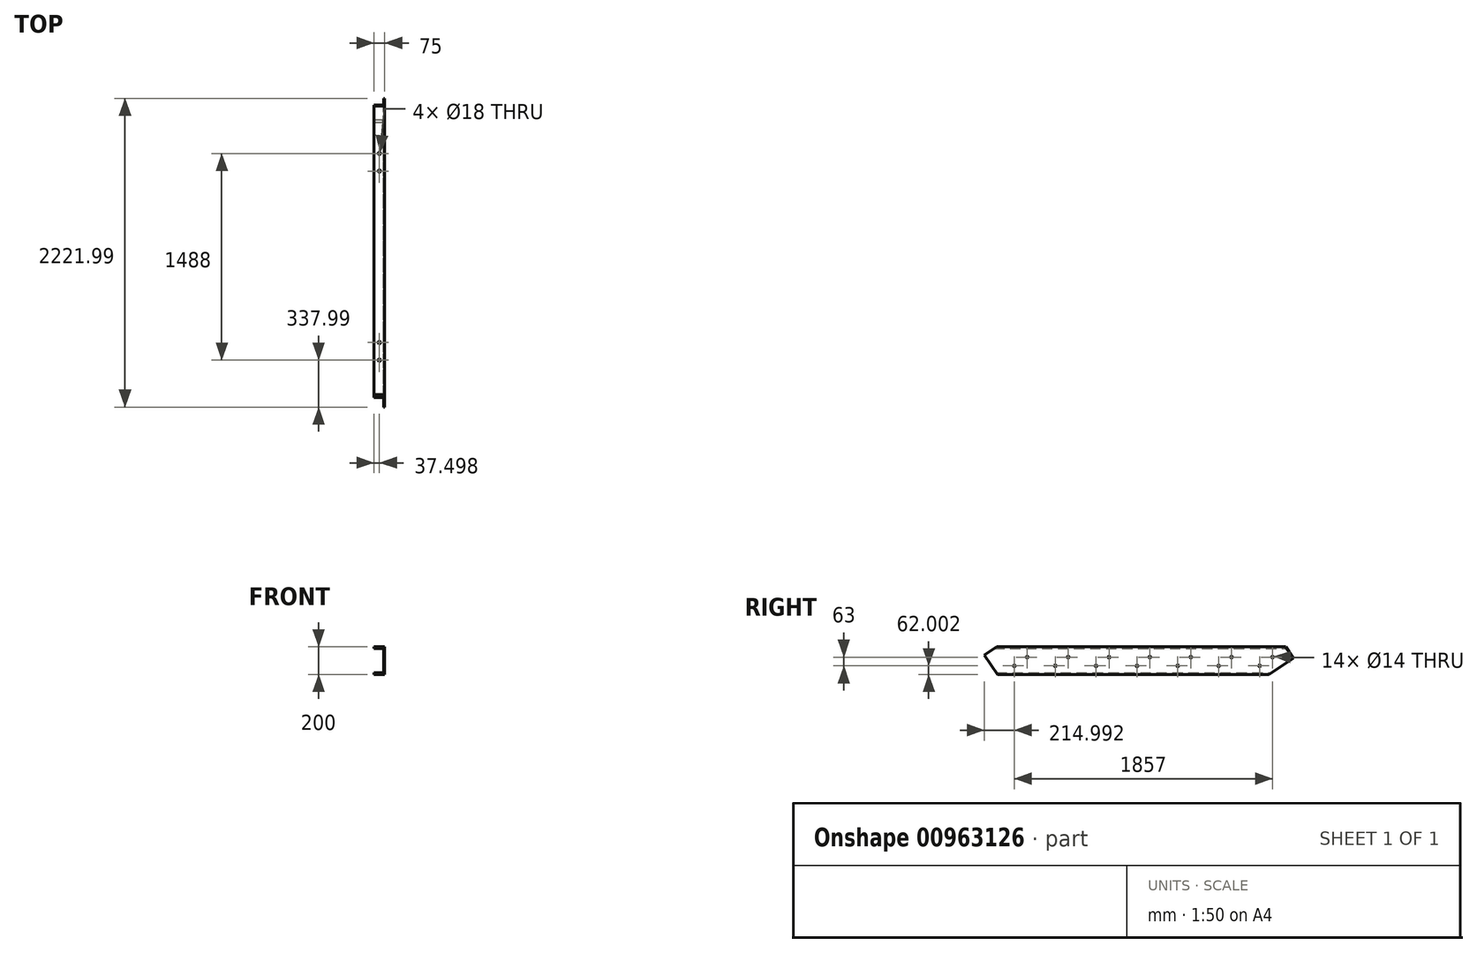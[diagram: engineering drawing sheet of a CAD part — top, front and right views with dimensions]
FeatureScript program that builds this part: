
annotation { "Feature Type Name" : "Feature", "Feature Type Description" : "" }
export const myFeature = defineFeature(function(context is Context, id is Id, definition is map)
    precondition{}
    {
        {
            var Q0;
            Q0=qCreatedBy(makeId("Front.planeOp"),FACE);
            var sketch = newSketch(context, id + "F0", { "sketchPlane" : qUnion([Q0])});
            skLineSegment(sketch, "E0", {"start": v(-161.38, 109) * mm, "end": v(-86.38, 109) * mm});
            skLineSegment(sketch, "E1", {"start": v(-86.38, 109) * mm, "end": v(-86.38, -91) * mm});
            skLineSegment(sketch, "E2", {"start": v(-86.38, -91) * mm, "end": v(-161.38, -91) * mm});
            skLineSegment(sketch, "E3.0", {"start": v(-92.38, 84.5) * mm, "end": v(-92.38, -66.5) * mm});
            skLineSegment(sketch, "E4.0", {"start": v(-161.38, 96.5) * mm, "end": v(-104.38, 96.5) * mm});
            skLineSegment(sketch, "E5.0", {"start": v(-104.38, -78.5) * mm, "end": v(-161.38, -78.5) * mm});
            skLineSegment(sketch, "E6", {"start": v(-161.38, 109) * mm, "end": v(-161.38, 96.5) * mm});
            skLineSegment(sketch, "E7", {"start": v(-161.38, -78.5) * mm, "end": v(-161.38, -91) * mm});
            skArc(sketch, "E8.filletArc", {"start": v(-104.38, -78.5) * mm, "mid": v(-95.9, -74.98) * mm, "end": v(-92.38, -66.5) * mm});
            skArc(sketch, "E9.filletArc", {"start": v(-92.38, 84.5) * mm, "mid": v(-95.9, 93) * mm, "end": v(-104.38, 96.5) * mm});
            skSolve(sketch);
        }
        {
            var Q0;
            Q0 = qSketchRegion(id + "F0", true);
            extrude(context, id + "F1", {"entities" : qUnion([Q0]), "depth" : 2222 * mm, "offsetDistance" : 25 * mm});
        }
        {
            var Q0;
            Q0=makeQuery(id+"F1.opExtrude","SWEPT_FACE",FACE,{"disambiguationData":[OSD([sQuery(id+"F0.wireOp",EDGE,"E7")])]});
            var sketch = newSketch(context, id + "F2", { "sketchPlane" : qUnion([Q0])});
            skLineSegment(sketch, "E10", {"start": v(0, 109.01) * mm, "end": v(0, 26.01) * mm});
            skLineSegment(sketch, "E11", {"start": v(0, 109.01) * mm, "end": v(56, 109.01) * mm});
            skLineSegment(sketch, "E12", {"start": v(56, 109.01) * mm, "end": v(0, 26.01) * mm});
            skLineSegment(sketch, "E13", {"start": v(0, -90.99) * mm, "end": v(174, -90.99) * mm});
            skLineSegment(sketch, "E14", {"start": v(174, -90.99) * mm, "end": v(0, 26.01) * mm});
            skLineSegment(sketch, "E15", {"start": v(0, 109.01) * mm, "end": v(150, 109.01) * mm});
            skLineSegment(sketch, "E16", {"start": v(150, 109.01) * mm, "end": v(243, 109.01) * mm});
            skCircle(sketch, "E17", {"center": v(150, 34.01) * mm, "radius": 7 * mm});
            skCircle(sketch, "E18", {"center": v(243, -28.99) * mm, "radius": 7 * mm});
            skCircle(sketch, "E19.1.0.0", {"center": v(444, 34.01) * mm, "radius": 7 * mm});
            skCircle(sketch, "E19.1.0.1", {"center": v(537, -28.99) * mm, "radius": 7 * mm});
            skCircle(sketch, "E19.2.0.0", {"center": v(738, 34.01) * mm, "radius": 7 * mm});
            skCircle(sketch, "E19.2.0.1", {"center": v(831, -28.99) * mm, "radius": 7 * mm});
            skCircle(sketch, "E19.3.0.0", {"center": v(1032, 34.01) * mm, "radius": 7 * mm});
            skCircle(sketch, "E19.3.0.1", {"center": v(1125, -28.99) * mm, "radius": 7 * mm});
            skCircle(sketch, "E19.4.0.0", {"center": v(1326, 34.01) * mm, "radius": 7 * mm});
            skCircle(sketch, "E19.4.0.1", {"center": v(1419, -28.99) * mm, "radius": 7 * mm});
            skCircle(sketch, "E19.5.0.0", {"center": v(1620, 34.01) * mm, "radius": 7 * mm});
            skCircle(sketch, "E19.5.0.1", {"center": v(1713, -28.99) * mm, "radius": 7 * mm});
            skCircle(sketch, "E19.6.0.0", {"center": v(1914, 34.01) * mm, "radius": 7 * mm});
            skCircle(sketch, "E19.6.0.1", {"center": v(2007, -28.99) * mm, "radius": 7 * mm});
            skLineSegment(sketch, "E19.direction1", {"start": v(150, 34.01) * mm, "end": v(444, 34.01) * mm, "construction": true});
            skLineSegment(sketch, "E20", {"start": v(2222, 109.01) * mm, "end": v(2134, 109.01) * mm});
            skLineSegment(sketch, "E21", {"start": v(2222, 109.01) * mm, "end": v(2222, 50.01) * mm});
            skLineSegment(sketch, "E22", {"start": v(2222, 50.01) * mm, "end": v(2134, 109.01) * mm});
            skLineSegment(sketch, "E23", {"start": v(2222, -90.99) * mm, "end": v(2127, -90.99) * mm});
            skLineSegment(sketch, "E24", {"start": v(2127, -90.99) * mm, "end": v(2222, 50.01) * mm});
            skLineSegment(sketch, "E25", {"start": v(0, 26.01) * mm, "end": v(0, -90.99) * mm});
            skLineSegment(sketch, "E26", {"start": v(2222, 50.01) * mm, "end": v(2222, -90.99) * mm});
            skSolve(sketch);
        }
        {
            var Q0;
            {var subQ0=sQuery(id+"F2.wireOp",EDGE,"E10");Q0=makeQuery(id+"F2.imprint","IMPRINT",FACE,{"disambiguationData":[TD([[makeQuery(id+"F2.imprint","IMPRINT",EDGE,{"derivedFrom":subQ0}),1.0]])]});}
            var Q1;
            {var subQ1=sQuery(id+"F2.wireOp",EDGE,"E14");var subQ3=makeQuery(id+"F1.opExtrude","SWEPT_EDGE",EDGE,{"disambiguationData":[OSD([sQuery(id+"F0.wireOp",EDGE,"E5.0"),sQuery(id+"F0.wireOp",EDGE,"E7")])]});var subQ4=makeQuery(id+"F2.imprint","INTERSECT",VERTEX,{"derivedFrom":[subQ3,subQ1]});Q1=makeQuery(id+"F2.imprint","IMPRINT",FACE,{"disambiguationData":[TD([[makeQuery(id+"F2.imprint","IMPRINT",EDGE,{"disambiguationData":[TD([[subQ4,-1.0]])],"derivedFrom":subQ1}),1.0]])]});}
            var Q2;
            {var subQ0=sQuery(id+"F2.wireOp",EDGE,"E13");Q2=makeQuery(id+"F2.imprint","IMPRINT",FACE,{"disambiguationData":[TD([[makeQuery(id+"F2.imprint","IMPRINT",EDGE,{"derivedFrom":subQ0}),1.0]])]});}
            var Q3;
            Q3=makeQuery(id+"F2.imprint","IMPRINT",FACE,{"disambiguationData":[TD([[makeQuery(id+"F2.imprint","IMPRINT",EDGE,{"derivedFrom":sQuery(id+"F2.wireOp",EDGE,"E17")}),1.0]])]});
            var Q4;
            Q4=makeQuery(id+"F2.imprint","IMPRINT",FACE,{"disambiguationData":[TD([[makeQuery(id+"F2.imprint","IMPRINT",EDGE,{"derivedFrom":sQuery(id+"F2.wireOp",EDGE,"E18")}),1.0]])]});
            var Q5;
            Q5=makeQuery(id+"F2.imprint","IMPRINT",FACE,{"disambiguationData":[TD([[makeQuery(id+"F2.imprint","IMPRINT",EDGE,{"derivedFrom":sQuery(id+"F2.wireOp",EDGE,"E19.1.0.0")}),1.0]])]});
            var Q6;
            Q6=makeQuery(id+"F2.imprint","IMPRINT",FACE,{"disambiguationData":[TD([[makeQuery(id+"F2.imprint","IMPRINT",EDGE,{"derivedFrom":sQuery(id+"F2.wireOp",EDGE,"E19.1.0.1")}),1.0]])]});
            var Q7;
            Q7=makeQuery(id+"F2.imprint","IMPRINT",FACE,{"disambiguationData":[TD([[makeQuery(id+"F2.imprint","IMPRINT",EDGE,{"derivedFrom":sQuery(id+"F2.wireOp",EDGE,"E19.2.0.0")}),1.0]])]});
            var Q8;
            Q8=makeQuery(id+"F2.imprint","IMPRINT",FACE,{"disambiguationData":[TD([[makeQuery(id+"F2.imprint","IMPRINT",EDGE,{"derivedFrom":sQuery(id+"F2.wireOp",EDGE,"E19.2.0.1")}),1.0]])]});
            var Q9;
            Q9=makeQuery(id+"F2.imprint","IMPRINT",FACE,{"disambiguationData":[TD([[makeQuery(id+"F2.imprint","IMPRINT",EDGE,{"derivedFrom":sQuery(id+"F2.wireOp",EDGE,"E19.3.0.0")}),1.0]])]});
            var Q10;
            Q10=makeQuery(id+"F2.imprint","IMPRINT",FACE,{"disambiguationData":[TD([[makeQuery(id+"F2.imprint","IMPRINT",EDGE,{"derivedFrom":sQuery(id+"F2.wireOp",EDGE,"E19.3.0.1")}),1.0]])]});
            var Q11;
            Q11=makeQuery(id+"F2.imprint","IMPRINT",FACE,{"disambiguationData":[TD([[makeQuery(id+"F2.imprint","IMPRINT",EDGE,{"derivedFrom":sQuery(id+"F2.wireOp",EDGE,"E20")}),1.0]])]});
            var Q12;
            {var subQ0=sQuery(id+"F2.wireOp",EDGE,"E26");Q12=makeQuery(id+"F2.imprint","IMPRINT",FACE,{"disambiguationData":[TD([[makeQuery(id+"F2.imprint","IMPRINT",EDGE,{"derivedFrom":subQ0}),-1.0]])]});}
            var Q13;
            {var subQ0=sQuery(id+"F2.wireOp",EDGE,"E24");var subQ1=sQuery(id+"F2.wireOp",EDGE,"E23");var subQ2=makeQuery(id+"F2.imprint","INTERSECT",VERTEX,{"derivedFrom":[subQ1,subQ0]});Q13=makeQuery(id+"F2.imprint","IMPRINT",FACE,{"disambiguationData":[TD([[makeQuery(id+"F2.imprint","IMPRINT",EDGE,{"disambiguationData":[TD([[subQ2,1.0]])],"derivedFrom":subQ1}),-1.0]])]});}
            var Q14;
            Q14=makeQuery(id+"F2.imprint","IMPRINT",FACE,{"disambiguationData":[TD([[makeQuery(id+"F2.imprint","IMPRINT",EDGE,{"derivedFrom":sQuery(id+"F2.wireOp",EDGE,"E19.6.0.1")}),1.0]])]});
            var Q15;
            Q15=makeQuery(id+"F2.imprint","IMPRINT",FACE,{"disambiguationData":[TD([[makeQuery(id+"F2.imprint","IMPRINT",EDGE,{"derivedFrom":sQuery(id+"F2.wireOp",EDGE,"E19.6.0.0")}),1.0]])]});
            var Q16;
            Q16=makeQuery(id+"F2.imprint","IMPRINT",FACE,{"disambiguationData":[TD([[makeQuery(id+"F2.imprint","IMPRINT",EDGE,{"derivedFrom":sQuery(id+"F2.wireOp",EDGE,"E19.5.0.1")}),1.0]])]});
            var Q17;
            Q17=makeQuery(id+"F2.imprint","IMPRINT",FACE,{"disambiguationData":[TD([[makeQuery(id+"F2.imprint","IMPRINT",EDGE,{"derivedFrom":sQuery(id+"F2.wireOp",EDGE,"E19.4.0.1")}),1.0]])]});
            var Q18;
            Q18=makeQuery(id+"F2.imprint","IMPRINT",FACE,{"disambiguationData":[TD([[makeQuery(id+"F2.imprint","IMPRINT",EDGE,{"derivedFrom":sQuery(id+"F2.wireOp",EDGE,"E19.4.0.0")}),1.0]])]});
            var Q19;
            Q19=makeQuery(id+"F2.imprint","IMPRINT",FACE,{"disambiguationData":[TD([[makeQuery(id+"F2.imprint","IMPRINT",EDGE,{"derivedFrom":sQuery(id+"F2.wireOp",EDGE,"E19.5.0.0")}),1.0]])]});
            extrude(context, id + "F3", {"entities" : qUnion([Q0, Q1, Q2, Q3, Q4, Q5, Q6, Q7, Q8, Q9, Q10, Q11, Q12, Q13, Q14, Q15, Q16, Q17, Q18, Q19]), "operationType" : NewBodyOperationType.REMOVE, "endBound" : BoundingType.THROUGH_ALL, "oppositeDirection" : true, "depth" : 25 * mm, "offsetDistance" : 25 * mm});
        }
        {
            var Q0;
            Q0=makeQuery(id+"F1.opExtrude","SWEPT_FACE",FACE,{"disambiguationData":[OSD([sQuery(id+"F0.wireOp",EDGE,"E0")])]});
            var sketch = newSketch(context, id + "F4", { "sketchPlane" : qUnion([Q0])});
            skLineSegment(sketch, "E27", {"start": v(-161.38, -2134) * mm, "end": v(-161.38, -1884) * mm, "construction": true});
            skLineSegment(sketch, "E28", {"start": v(-161.38, -1884) * mm, "end": v(-123.88, -1884) * mm, "construction": true});
            skLineSegment(sketch, "E29", {"start": v(-123.88, -1884) * mm, "end": v(-123.88, -1839) * mm, "construction": true});
            skLineSegment(sketch, "E30", {"start": v(-123.88, -1839) * mm, "end": v(-123.88, -1757) * mm, "construction": true});
            skCircle(sketch, "E31", {"center": v(-123.88, -1884) * mm, "radius": 9 * mm});
            skCircle(sketch, "E32", {"center": v(-123.88, -1757) * mm, "radius": 9 * mm});
            skLineSegment(sketch, "E33", {"start": v(-161.38, -56) * mm, "end": v(-161.38, -396) * mm, "construction": true});
            skLineSegment(sketch, "E34", {"start": v(-161.38, -396) * mm, "end": v(-123.88, -396) * mm, "construction": true});
            skLineSegment(sketch, "E35", {"start": v(-123.88, -396) * mm, "end": v(-123.88, -441) * mm, "construction": true});
            skLineSegment(sketch, "E36", {"start": v(-123.88, -441) * mm, "end": v(-123.88, -523) * mm, "construction": true});
            skCircle(sketch, "E37", {"center": v(-123.88, -523) * mm, "radius": 9 * mm});
            skCircle(sketch, "E38", {"center": v(-123.88, -396) * mm, "radius": 9 * mm});
            skSolve(sketch);
        }
        {
            var Q0;
            Q0 = qSketchRegion(id + "F4", true);
            extrude(context, id + "F5", {"entities" : qUnion([Q0]), "operationType" : NewBodyOperationType.REMOVE, "endBound" : BoundingType.UP_TO_NEXT, "oppositeDirection" : true, "depth" : 25 * mm, "offsetDistance" : 25 * mm});
        }
    });
